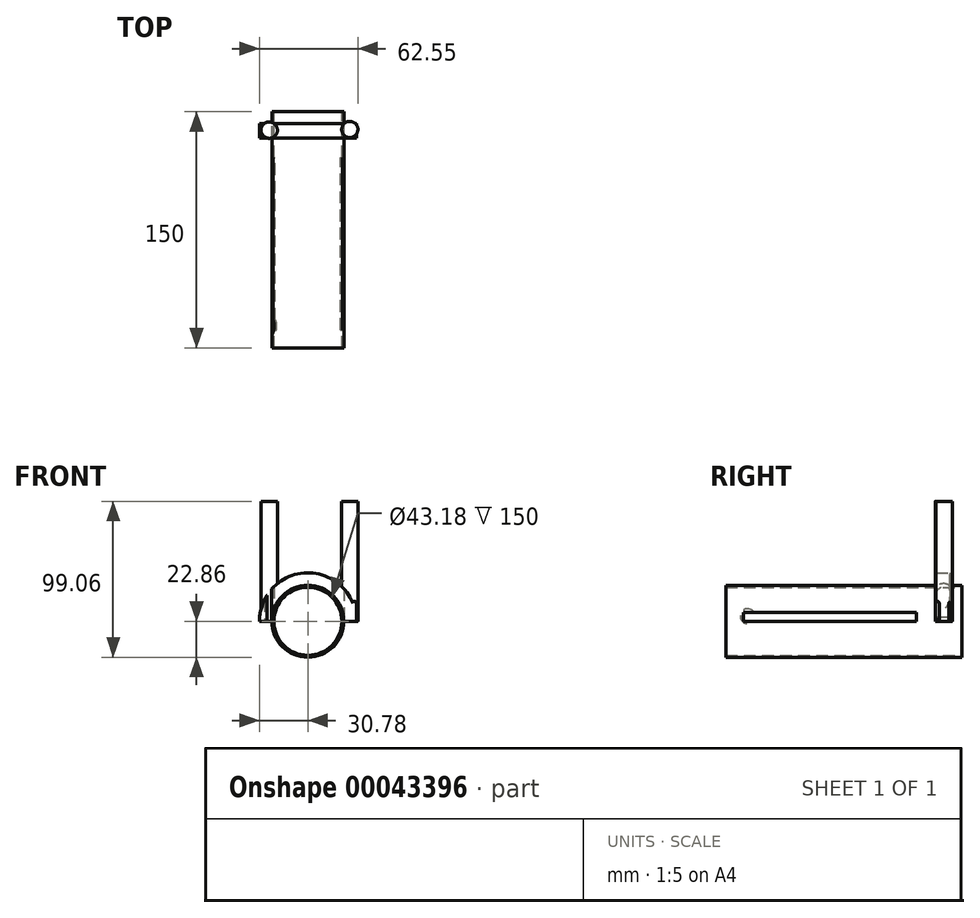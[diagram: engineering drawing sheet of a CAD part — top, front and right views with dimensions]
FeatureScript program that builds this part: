
annotation { "Feature Type Name" : "Feature", "Feature Type Description" : "" }
export const myFeature = defineFeature(function(context is Context, id is Id, definition is map)
    precondition{}
    {
        {
            var Q0;
            Q0=qCreatedBy(makeId("Front.planeOp"),FACE);
            var sketch = newSketch(context, id + "F0", { "sketchPlane" : qUnion([Q0])});
            skCircle(sketch, "E0", {"center": v(0, 0) * mm, "radius": 22.86 * mm});
            skCircle(sketch, "E1", {"center": v(0, 0) * mm, "radius": 21.59 * mm});
            skSolve(sketch);
        }
        {
            var Q0;
            Q0=makeQuery(id+"F0.imprint","IMPRINT",FACE,{"disambiguationData":[TD([[makeQuery(id+"F0.imprint","IMPRINT",EDGE,{"derivedFrom":sQuery(id+"F0.wireOp",EDGE,"E0")}),1.0]])]});
            extrude(context, id + "F1", {"entities" : qUnion([Q0]), "depth" : 150 * mm});
        }
        {
            var Q0;
            Q0=qCreatedBy(makeId("Right.planeOp"),FACE);
            var sketch = newSketch(context, id + "F2", { "sketchPlane" : qUnion([Q0])});
            skLineSegment(sketch, "E2.bottom", {"start": v(-29.04, 0) * mm, "end": v(-138.66, 0) * mm});
            skLineSegment(sketch, "E2.top", {"start": v(-29.04, 5.72) * mm, "end": v(-138.66, 5.72) * mm});
            skLineSegment(sketch, "E2.left", {"start": v(-29.04, 0) * mm, "end": v(-29.04, 5.72) * mm});
            skLineSegment(sketch, "E2.right", {"start": v(-138.66, 0) * mm, "end": v(-138.66, 5.72) * mm});
            skSolve(sketch);
        }
        {
            var Q0;
            Q0=qSketchRegion(id+"F2",true);
            extrude(context, id + "F3", {"entities" : qUnion([Q0]), "operationType" : NewBodyOperationType.REMOVE, "endBound" : BoundingType.SYMMETRIC, "oppositeDirection" : true, "depth" : 76.2 * mm});
        }
        {
            var Q0;
            Q0=qCreatedBy(makeId("Top.planeOp"),FACE);
            var sketch = newSketch(context, id + "F4", { "sketchPlane" : qUnion([Q0])});
            skLineSegment(sketch, "E3.bottom", {"start": v(14.56, -7.58) * mm, "end": v(30.78, -7.58) * mm});
            skLineSegment(sketch, "E3.top", {"start": v(14.56, -16.73) * mm, "end": v(30.78, -16.73) * mm});
            skLineSegment(sketch, "E3.left", {"start": v(14.56, -7.58) * mm, "end": v(14.56, -16.73) * mm});
            skLineSegment(sketch, "E3.right", {"start": v(30.78, -7.58) * mm, "end": v(30.78, -16.73) * mm});
            skSolve(sketch);
        }
        {
            var Q0;
            Q0=qSketchRegion(id+"F4",true);
            extrude(context, id + "F5", {"entities" : qUnion([Q0]), "operationType" : NewBodyOperationType.ADD, "depth" : 12.7 * mm});
        }
        {
            var Q0;
            {var subQ0=sQuery(id+"F4.wireOp",EDGE,"E3.right");var subQ1=sQuery(id+"F0B8wNnZoACMYPZ_1.wireOp",EDGE,"0657b783-154f-4117-873f-c8229050e505");Q0=makeQuery(id+"FjSrg42h6ONFkE3_1.boolean.opBoolean","SPLIT",EDGE,{"disambiguationData":[TD([makeQuery(id+"F5.opExtrude","CAP_FACE",FACE,{"disambiguationData":[OSD([sQuery(id+"F4.wireOp",EDGE,"E3.bottom"),sQuery(id+"F4.wireOp",EDGE,"E3.top"),sQuery(id+"F4.wireOp",EDGE,"E3.left"),subQ0])],"isStart":true}),makeQuery(id+"F5.opExtrude","SWEPT_FACE",FACE,{"disambiguationData":[OSD([subQ0])]}),makeQuery(id+"FjSrg42h6ONFkE3_1.opExtrude","SWEPT_FACE",FACE,{"disambiguationData":[OSD([subQ1])]}),makeQuery(id+"FjSrg42h6ONFkE3_1.opExtrude","CAP_FACE",FACE,{"disambiguationData":[OSD([subQ1])],"isStart":true})])],"derivedFrom":makeQuery(id+"F5.opExtrude","CAP_EDGE",EDGE,{"disambiguationData":[OSD([subQ0])],"isStart":true})});}
            var Q1;
            Q1=makeQuery(id+"F5.opExtrude","CAP_EDGE",EDGE,{"disambiguationData":[OSD([sQuery(id+"F4.wireOp",EDGE,"E3.left")])],"isStart":false});
            var Q2;
            Q2=makeQuery(id+"F5.opExtrude","CAP_EDGE",EDGE,{"disambiguationData":[OSD([sQuery(id+"F4.wireOp",EDGE,"E3.top")])],"isStart":false});
            var Q3;
            Q3=makeQuery(id+"F5.opExtrude","CAP_EDGE",EDGE,{"disambiguationData":[OSD([sQuery(id+"F4.wireOp",EDGE,"E3.bottom")])],"isStart":false});
            var Q4;
            Q4=makeQuery(id+"F5.opExtrude","CAP_EDGE",EDGE,{"disambiguationData":[OSD([sQuery(id+"F4.wireOp",EDGE,"E3.right")])],"isStart":false});
            fillet(context, id + "F6", {"entities" : qUnion([Q0, Q1, Q2, Q3, Q4]), "radius" : 1.27 * mm, "tangentPropagation" : true, "allowEdgeOverflow" : false});
        }
        {
            var Q0;
            Q0=qSketchRegion(id+"F4",true);
            var Q1;
            Q1=makeQuery(id+"F1.opExtrude","CAP_EDGE",EDGE,{"disambiguationData":[OSD([sQuery(id+"F0.wireOp",EDGE,"E0")])],"isStart":true});
            revolve(context, id + "F7", {"operationType" : NewBodyOperationType.ADD, "entities" : qUnion([Q0]), "axis" : qUnion([Q1]), "revolveType" : RevolveType.ONE_DIRECTION, "angle" : 180 * degree});
        }
        {
            var Q0;
            Q0=qCreatedBy(makeId("Top.planeOp"),FACE);
            var sketch = newSketch(context, id + "F8", { "sketchPlane" : qUnion([Q0])});
            skCircle(sketch, "E4", {"center": v(-24.54, -11.74) * mm, "radius": 5.21 * mm});
            skCircle(sketch, "E5", {"center": v(26.62, -11.32) * mm, "radius": 5.15 * mm});
            skSolve(sketch);
        }
        {
            var Q0;
            Q0=qSketchRegion(id+"F8",true);
            extrude(context, id + "F9", {"entities" : qUnion([Q0]), "operationType" : NewBodyOperationType.ADD, "depth" : 76.2 * mm});
        }
        {
            var Q0;
            Q0=qCreatedBy(makeId("Right.planeOp"),FACE);
            var sketch = newSketch(context, id + "F10", { "sketchPlane" : qUnion([Q0])});
            skCircle(sketch, "E6", {"center": v(-136.1, 3.22) * mm, "radius": 4.7 * mm});
            skSolve(sketch);
        }
        {
            var Q0;
            Q0=qSketchRegion(id+"F10",true);
            extrude(context, id + "F11", {"entities" : qUnion([Q0]), "operationType" : NewBodyOperationType.REMOVE, "oppositeDirection" : true, "depth" : 25.4 * mm});
        }
        {
            var Q0;
            {var subQ0=sQuery(id+"F4.wireOp",EDGE,"E3.bottom");Q0=makeQuery(id+"F7.boolean.opBoolean","MERGE",FACE,{"derivedFrom":[makeQuery(id+"F5.boolean.opBoolean","SPLIT",FACE,{"disambiguationData":[TD([makeQuery(id+"F1.opExtrude","SWEPT_FACE",FACE,{"disambiguationData":[OSD([sQuery(id+"F0.wireOp",EDGE,"E1")])]})])],"derivedFrom":makeQuery(id+"F5.opExtrude","SWEPT_FACE",FACE,{"disambiguationData":[OSD([subQ0])]})}),makeQuery(id+"F7.opRevolve","SWEPT_FACE",FACE,{"disambiguationData":[OSD([subQ0])]})]});}
            extrude(context, id + "F12", {"entities" : qUnion([Q0]), "operationType" : NewBodyOperationType.REMOVE, "endBound" : BoundingType.SYMMETRIC, "oppositeDirection" : true, "depth" : 25.4 * mm});
        }
    });
